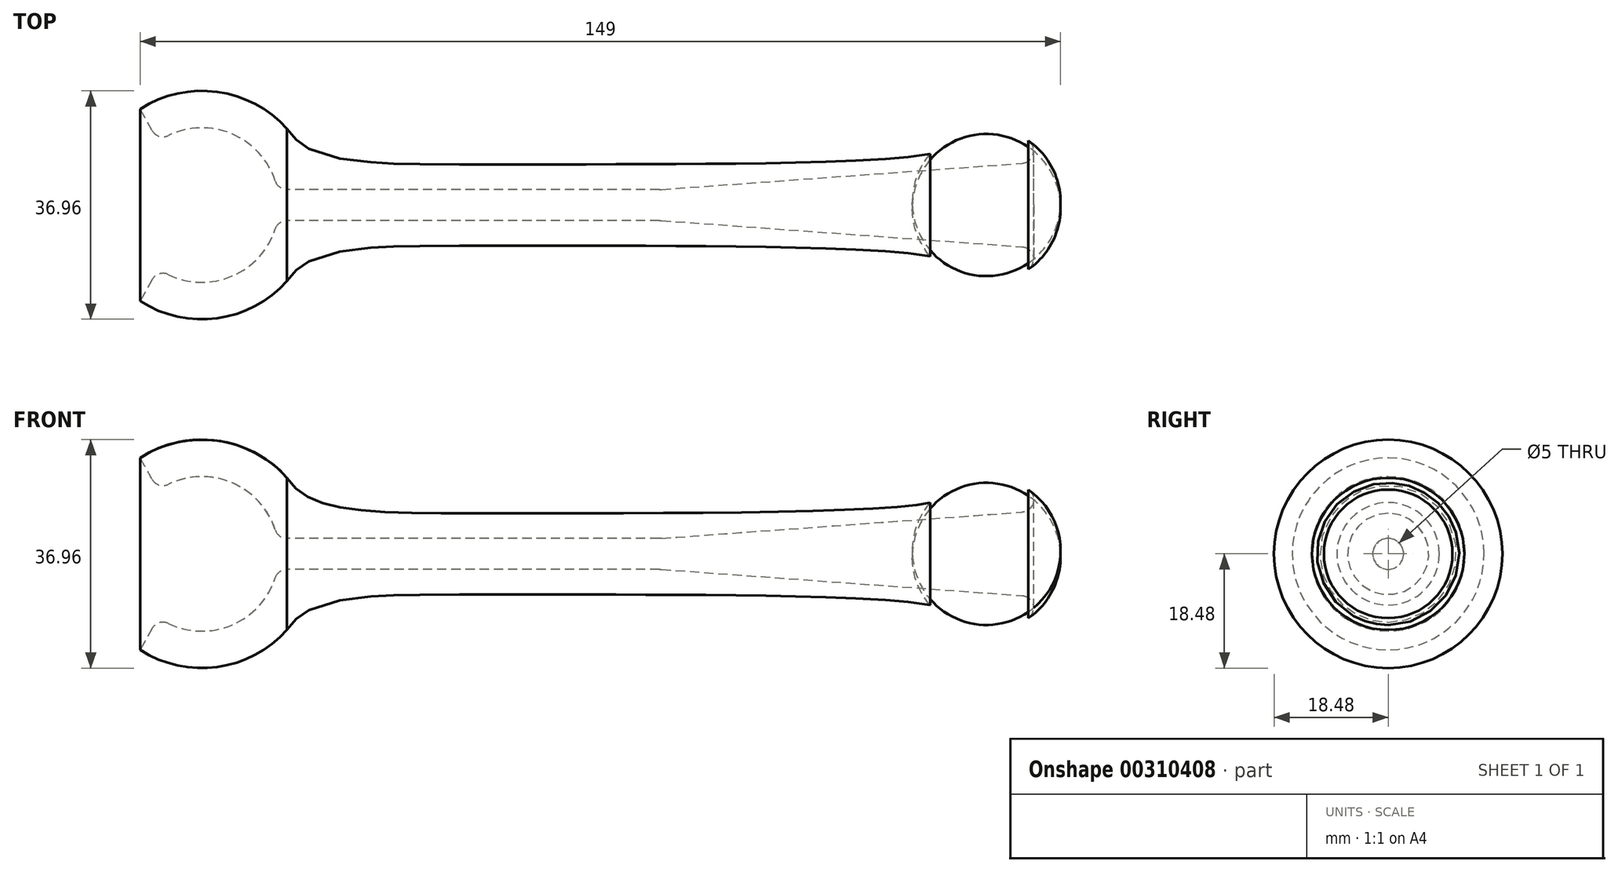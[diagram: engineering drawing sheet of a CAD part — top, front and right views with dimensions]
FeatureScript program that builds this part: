
annotation { "Feature Type Name" : "Feature", "Feature Type Description" : "" }
export const myFeature = defineFeature(function(context is Context, id is Id, definition is map)
    precondition{}
    {
        {
            var Q0;
            Q0=qCreatedBy(makeId("Front.planeOp"),FACE);
            var sketch = newSketch(context, id + "F0", { "sketchPlane" : qUnion([Q0])});
            skLineSegment(sketch, "E0", {"start": v(12.5, 0) * mm, "end": v(57.5, 0) * mm});
            skArc(sketch, "E1", {"start": v(12.25, 2.5) * mm, "mid": v(4.69, 11.59) * mm, "end": v(-7.07, 10.3) * mm});
            skFitSpline(sketch, "E2", {"points": [v(13.78, 12.32) * mm, v(44.08, 6.6) * mm, v(117.88, 8.3) * mm], "startDerivative": vector(27.08, -44.66) * mm, "endDerivative": vector(40.46, 9.5) * mm});
            skLineSegment(sketch, "E3", {"start": v(12.25, 2.5) * mm, "end": v(74.25, 2.5) * mm});
            skLineSegment(sketch, "E4", {"start": v(74.25, 2.5) * mm, "end": v(137.04, 7.07) * mm});
            skArc(sketch, "E5.trimOffspring", {"start": v(137.04, 7.07) * mm, "mid": v(127.77, 12.47) * mm, "end": v(117.88, 8.3) * mm});
            skPoint(sketch, "E6.end.orphan", {"position": v(82.25, 2.5) * mm});
            skPoint(sketch, "E7.orphan", {"position": v(82.5, 0) * mm});
            skArc(sketch, "E8", {"start": v(13.78, 12.32) * mm, "mid": v(2.48, 18.32) * mm, "end": v(-10, 15.54) * mm});
            skLineSegment(sketch, "E9", {"start": v(-7.07, 10.3) * mm, "end": v(-10, 15.54) * mm});
            skLineSegment(sketch, "E10", {"start": v(0, 0) * mm, "end": v(127, 0.5) * mm, "construction": true});
            skSolve(sketch);
        }
        {
            var Q0;
            Q0=makeQuery(id+"F0.imprint","IMPRINT",FACE,{"disambiguationData":[TD([[makeQuery(id+"F0.imprint","IMPRINT",EDGE,{"derivedFrom":sQuery(id+"F0.wireOp",EDGE,"E1")}),-1.0]])]});
            var Q1;
            Q1=sQuery(id+"F0.wireOp",EDGE,"E0");
            revolve(context, id + "F1", {"entities" : qUnion([Q0]), "axis" : qUnion([Q1]), "revolveType" : RevolveType.FULL});
        }
        {
            var Q0;
            Q0=makeQuery(id+"F1.opRevolve","SWEPT_EDGE",EDGE,{"disambiguationData":[OSD([sQuery(id+"F0.wireOp",EDGE,"E1"),sQuery(id+"F0.wireOp",EDGE,"CbFEBDJi-CplH-pibZ-NPAv-z09MQRNn6UNR")])]});
            var Q1;
            Q1=makeQuery(id+"F1.opRevolve","SWEPT_EDGE",EDGE,{"disambiguationData":[OSD([sQuery(id+"F0.wireOp",EDGE,"E4"),sQuery(id+"F0.wireOp",EDGE,"E5.trimOffspring")])]});
            fillet(context, id + "F2", {"entities" : qUnion([Q0, Q1]), "radius" : 2 * mm, "tangentPropagation" : true, "allowEdgeOverflow" : false});
        }
        {
            var Q0;
            Q0=makeQuery(id+"F1.opRevolve","SWEPT_EDGE",EDGE,{"disambiguationData":[OSD([sQuery(id+"F0.wireOp",EDGE,"E3"),sQuery(id+"F0.wireOp",EDGE,"E4")])]});
            fillet(context, id + "F3", {"entities" : qUnion([Q0]), "radius" : 5 * mm, "tangentPropagation" : true, "allowEdgeOverflow" : false});
        }
    });
